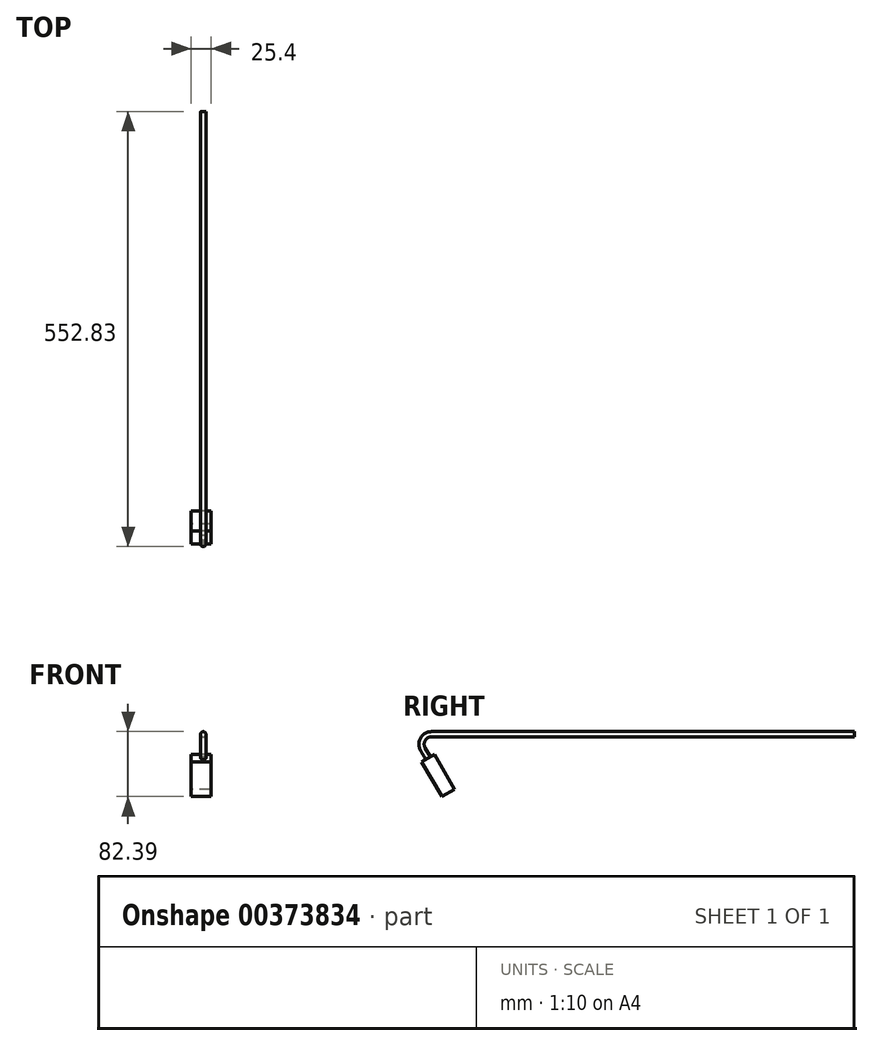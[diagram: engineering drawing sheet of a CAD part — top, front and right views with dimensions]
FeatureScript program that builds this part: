
annotation { "Feature Type Name" : "Feature", "Feature Type Description" : "" }
export const myFeature = defineFeature(function(context is Context, id is Id, definition is map)
    precondition{}
    {
        {
            var Q0;
            Q0=qCreatedBy(makeId("Right.planeOp"),FACE);
            var sketch = newSketch(context, id + "F0", { "sketchPlane" : qUnion([Q0])});
            skLineSegment(sketch, "E0", {"start": v(0, 0) * mm, "end": v(-25.4, 44) * mm});
            skLineSegment(sketch, "E1", {"start": v(-25.4, 44) * mm, "end": v(-41.46, 34.72) * mm});
            skLineSegment(sketch, "E2", {"start": v(-41.46, 34.72) * mm, "end": v(-16.06, -9.27) * mm});
            skLineSegment(sketch, "E3", {"start": v(-16.06, -9.27) * mm, "end": v(0, 0) * mm});
            skLineSegment(sketch, "E4", {"start": v(0, 0) * mm, "end": v(0, -57.51) * mm, "construction": true});
            skSolve(sketch);
        }
        {
            var Q0;
            Q0 = qSketchRegion(id + "F0", true);
            extrude(context, id + "F1", {"entities" : qUnion([Q0]), "depth" : 25.4 * mm});
        }
        {
            var Q0;
            Q0=qCreatedBy(makeId("Right.planeOp"),FACE);
            cPlane(context, id + "F2", {"entities" : qUnion([Q0]), "cplaneType" : CPlaneType.OFFSET, "offset" : 15.24 * mm, "width" : 152.4 * mm, "height" : 152.4 * mm});
        }
        {
            var Q0;
            Q0=qCreatedBy(id+"F2.planeOp",FACE);
            var sketch = newSketch(context, id + "F3", { "sketchPlane" : qUnion([Q0])});
            skLineSegment(sketch, "E5", {"start": v(-33.43, 39.36) * mm, "end": v(-40, 50.74) * mm});
            skLineSegment(sketch, "E6", {"start": v(-29, 69.79) * mm, "end": v(507.8, 69.79) * mm});
            skPoint(sketch, "E7.visualSharp", {"position": v(-51, 69.79) * mm});
            skArc(sketch, "E7.filletArc", {"start": v(-29, 69.79) * mm, "mid": v(-40, 63.44) * mm, "end": v(-40, 50.74) * mm});
            skSolve(sketch);
        }
        {
            var Q0;
            Q0=makeQuery(id+"F1.opExtrude","SWEPT_FACE",FACE,{"disambiguationData":[OSD([sQuery(id+"F0.wireOp",EDGE,"E1")])]});
            var sketch = newSketch(context, id + "F4", { "sketchPlane" : qUnion([Q0])});
            skCircle(sketch, "E8", {"center": v(15.24, -9.27) * mm, "radius": 3.33 * mm});
            skSolve(sketch);
        }
        {
            var Q0;
            Q0 = qSketchRegion(id + "F4", true);
            var Q1;
            Q1 = qConstructionFilter(qBodyType(qCreatedBy(id + "F3" ,EDGE), BodyType.WIRE), ConstructionObject.NO);
            sweep(context, id + "F5", {"operationType" : NewBodyOperationType.ADD, "profiles" : qUnion([Q0]), "path" : qUnion([Q1])});
        }
    });
